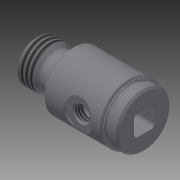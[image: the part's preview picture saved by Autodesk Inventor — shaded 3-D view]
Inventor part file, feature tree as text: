
AUTODESK INVENTOR PART (.ipt)
format: ipt  version: 2013 (Build 170138000, 138)  size: 262,144 bytes
history: native  units: in
note: dims shown in document units (in); Inventor stores cm internally (conversion verified against a paired STEP export)
features: other x119, sketch x5, revolve x4, thread x2, extrude x1
ambient origin geometry x8: Origin, YZ Plane, XZ Plane, XY Plane, X Axis, Y Axis, Z Axis, Center Point
bodies: Solid1 (feature_tree)
feature tree (131):
  revolve  "Revolution1"  [1 undecoded]
  thread  "Thread1"  [1 undecoded]
  revolve  "Revolution2"  [1 undecoded]
  revolve  "Revolution3"  [1 undecoded]
  thread  "Thread2"  [1 undecoded]
  revolve  "Revolution4"  [1 undecoded]
  extrude  "Extrusion1"  [1 undecoded]
  other  "m1_XY"
  other  "m1_YZ"
  other  "m1_ZX"
  other  "m1_X"
  other  "m1_Y"
  other  "m1_Z"
  other  "m1_Center"
  other  "m2_XY"
  other  "m2_YZ"
  other  "m2_ZX"
  other  "m2_X"
  other  "m2_Y"
  other  "m2_Z"
  other  "m2_Center"
  other  "s1_XY"
  other  "s1_YZ"
  other  "s1_ZX"
  other  "s1_X"
  other  "s1_Y"
  other  "s1_Z"
  other  "s1_Center"
  other  "s2_XY"
  other  "s2_YZ"
  other  "s2_ZX"
  other  "s2_X"
  other  "s2_Y"
  other  "s2_Z"
  other  "s2_Center"
  other  "dp1_XY"
  other  "dp1_YZ"
  other  "dp1_ZX"
  other  "dp1_X"
  other  "dp1_Y"
  other  "dp1_Z"
  other  "dp1_Center"
  other  "dp2_XY"
  other  "dp2_YZ"
  other  "dp2_ZX"
  other  "dp2_X"
  other  "dp2_Y"
  other  "dp2_Z"
  other  "dp2_Center"
  other  "rod_guide_XY"
  other  "rod_guide_YZ"
  other  "rod_guide_ZX"
  other  "rod_guide_X"
  other  "rod_guide_Y"
  other  "rod_guide_Z"
  other  "rod_guide_Center"
  other  "to_tube_XY"
  other  "to_tube_YZ"
  other  "to_tube_ZX"
  other  "to_tube_X"
  other  "to_tube_Y"
  other  "to_tube_Z"
  other  "to_tube_Center"
  other  "to_foot_bracket_XY"
  other  "to_foot_bracket_YZ"
  other  "to_foot_bracket_ZX"
  other  "to_foot_bracket_X"
  other  "to_foot_bracket_Y"
  other  "to_foot_bracket_Z"
  other  "to_foot_bracket_Center"
  other  "to_nut_XY"
  other  "to_nut_YZ"
  other  "to_nut_ZX"
  other  "to_nut_X"
  other  "to_nut_Y"
  other  "to_nut_Z"
  other  "to_nut_Center"
  other  "to_trunnion_brackets_XY"
  other  "to_trunnion_brackets_YZ"
  other  "to_trunnion_brackets_ZX"
  other  "to_trunnion_brackets_X"
  other  "to_trunnion_brackets_Y"
  other  "to_trunnion_brackets_Z"
  other  "to_trunnion_brackets_Center"
  other  "to_trunnion_brackets1_XY"
  other  "to_trunnion_brackets1_YZ"
  other  "to_trunnion_brackets1_ZX"
  other  "to_trunnion_brackets1_X"
  other  "to_trunnion_brackets1_Y"
  other  "to_trunnion_brackets1_Z"
  other  "to_trunnion_brackets1_Center"
  other  "to_trunnion_brackets2_XY"
  other  "to_trunnion_brackets2_YZ"
  other  "to_trunnion_brackets2_ZX"
  other  "to_trunnion_brackets2_X"
  other  "to_trunnion_brackets2_Y"
  other  "to_trunnion_brackets2_Z"
  other  "to_trunnion_brackets2_Center"
  other  "t1_XY"
  other  "t1_YZ"
  other  "t1_ZX"
  other  "t1_X"
  other  "t1_Y"
  other  "t1_Z"
  other  "t1_Center"
  other  "port_XY"
  other  "port_YZ"
  other  "port_ZX"
  other  "port_X"
  other  "port_Y"
  other  "port_Z"
  other  "port_Center"
  other  "rod_guide_1_XY"
  other  "rod_guide_1_YZ"
  other  "rod_guide_1_ZX"
  other  "rod_guide_1_X"
  other  "rod_guide_1_Y"
  other  "rod_guide_1_Z"
  other  "rod_guide_1_Center"
  other  "rod_guide_11_XY"
  other  "rod_guide_11_YZ"
  other  "rod_guide_11_ZX"
  other  "rod_guide_11_X"
  other  "rod_guide_11_Y"
  other  "rod_guide_11_Z"
  other  "rod_guide_11_Center"
  sketch  "Sketch_2"  dims[d0=360.0deg d1=0.1537in d2=0.0in d3=360.0deg]
  sketch  "Sketch_3"  dims[d4=360.0deg d5=0.0955in d6=0.212in]
  sketch  "Sketch_12"  dims[d7=360.0deg d8=2.312in d9=0.0in]
  sketch  "Sketch_47"
  sketch  "Sketch_33"
note: 7 required parameter values undecoded (feature->parameter linkage not recoverable at this tier; creation-order binding heuristic only, values carry confidence <= 0.55)